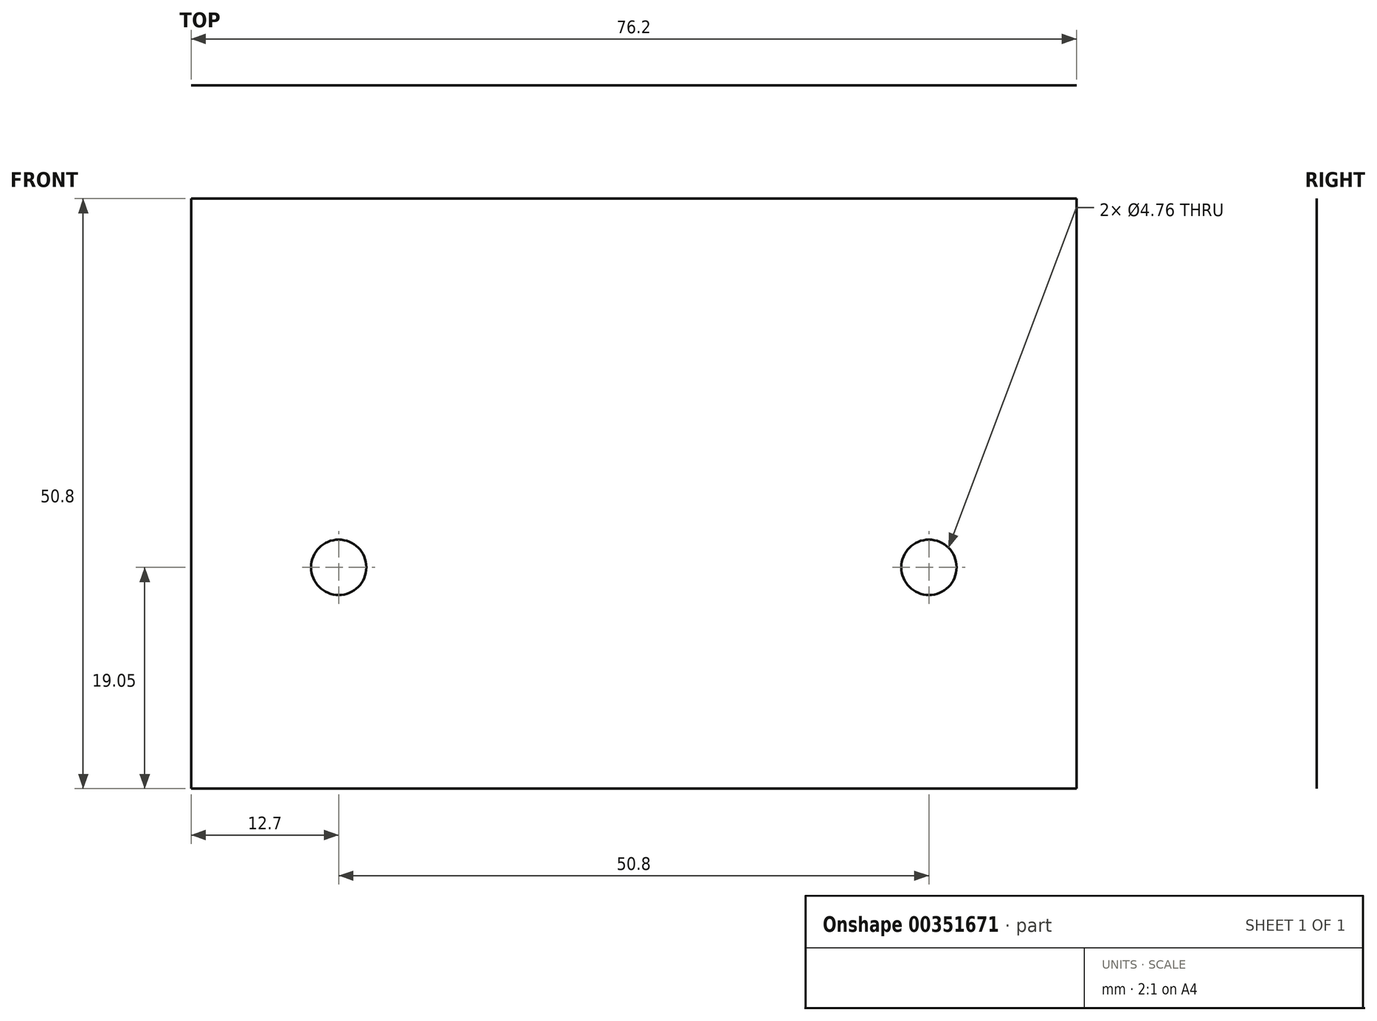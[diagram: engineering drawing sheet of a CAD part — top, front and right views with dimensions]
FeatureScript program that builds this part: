
annotation { "Feature Type Name" : "Feature", "Feature Type Description" : "" }
export const myFeature = defineFeature(function(context is Context, id is Id, definition is map)
    precondition{}
    {
        {
            var Q0;
            Q0=qCreatedBy(makeId("Front.planeOp"),FACE);
            var sketch = newSketch(context, id + "F0", { "sketchPlane" : qUnion([Q0])});
            skLineSegment(sketch, "E0.bottom", {"start": v(-38.1, 25.4) * mm, "end": v(38.1, 25.4) * mm});
            skLineSegment(sketch, "E0.top", {"start": v(-38.1, -25.4) * mm, "end": v(38.1, -25.4) * mm});
            skLineSegment(sketch, "E0.left", {"start": v(-38.1, 25.4) * mm, "end": v(-38.1, -25.4) * mm});
            skLineSegment(sketch, "E0.right", {"start": v(38.1, 25.4) * mm, "end": v(38.1, -25.4) * mm});
            skPoint(sketch, "E0.middle", {"position": v(0, 0) * mm});
            skSolve(sketch);
        }
        {
            var Q0;
            Q0=makeQuery(id+"F0.imprint","IMPRINT",FACE,{"disambiguationData":[TD([[makeQuery(id+"F0.imprint","IMPRINT",EDGE,{"derivedFrom":sQuery(id+"F0.wireOp",EDGE,"E0.bottom")}),-1.0]])]});
            extrude(context, id + "F1", {"entities" : qUnion([Q0]), "endBound" : BoundingType.SYMMETRIC, "depth" : 1 / 203.2 * mm});
        }
        {
            var Q0;
            Q0=makeQuery(id+"F1.opExtrude","CAP_FACE",FACE,{"disambiguationData":[OSD([sQuery(id+"F0.wireOp",EDGE,"E0.bottom"),sQuery(id+"F0.wireOp",EDGE,"E0.top"),sQuery(id+"F0.wireOp",EDGE,"E0.left"),sQuery(id+"F0.wireOp",EDGE,"E0.right")])],"isStart":false});
            var sketch = newSketch(context, id + "F2", { "sketchPlane" : qUnion([Q0])});
            skCircle(sketch, "E1", {"center": v(-25.4, -6.35) * mm, "radius": 2.38 * mm});
            skSolve(sketch);
        }
        {
            var Q0;
            Q0=makeQuery(id+"F2.imprint","IMPRINT",FACE,{"disambiguationData":[TD([[makeQuery(id+"F2.imprint","IMPRINT",EDGE,{"derivedFrom":sQuery(id+"F2.wireOp",EDGE,"E1")}),-1.0]])]});
            var sketch = newSketch(context, id + "F3", { "sketchPlane" : qUnion([Q0])});
            skCircle(sketch, "E2", {"center": v(25.4, -6.35) * mm, "radius": 2.38 * mm});
            skSolve(sketch);
        }
        {
            var Q0;
            Q0 = qSketchRegion(id + "F2", true);
            var Q1;
            Q1=makeQuery(id+"F1.opExtrude","CAP_FACE",FACE,{"disambiguationData":[OSD([sQuery(id+"F0.wireOp",EDGE,"E0.bottom"),sQuery(id+"F0.wireOp",EDGE,"E0.top"),sQuery(id+"F0.wireOp",EDGE,"E0.left"),sQuery(id+"F0.wireOp",EDGE,"E0.right")])],"isStart":true});
            extrude(context, id + "F4", {"entities" : qUnion([Q0]), "operationType" : NewBodyOperationType.REMOVE, "endBound" : BoundingType.UP_TO_SURFACE, "oppositeDirection" : true, "endBoundEntityFace" : qUnion([Q1]), "depth" : 25.4 * mm});
        }
        {
            var Q0;
            Q0 = qSketchRegion(id + "F3", true);
            var Q1;
            Q1=makeQuery(id+"F1.opExtrude","CAP_FACE",FACE,{"disambiguationData":[OSD([sQuery(id+"F0.wireOp",EDGE,"E0.bottom"),sQuery(id+"F0.wireOp",EDGE,"E0.top"),sQuery(id+"F0.wireOp",EDGE,"E0.left"),sQuery(id+"F0.wireOp",EDGE,"E0.right")])],"isStart":true});
            extrude(context, id + "F5", {"entities" : qUnion([Q0]), "operationType" : NewBodyOperationType.REMOVE, "endBound" : BoundingType.UP_TO_SURFACE, "oppositeDirection" : true, "endBoundEntityFace" : qUnion([Q1]), "depth" : 25.4 * mm});
        }
    });
